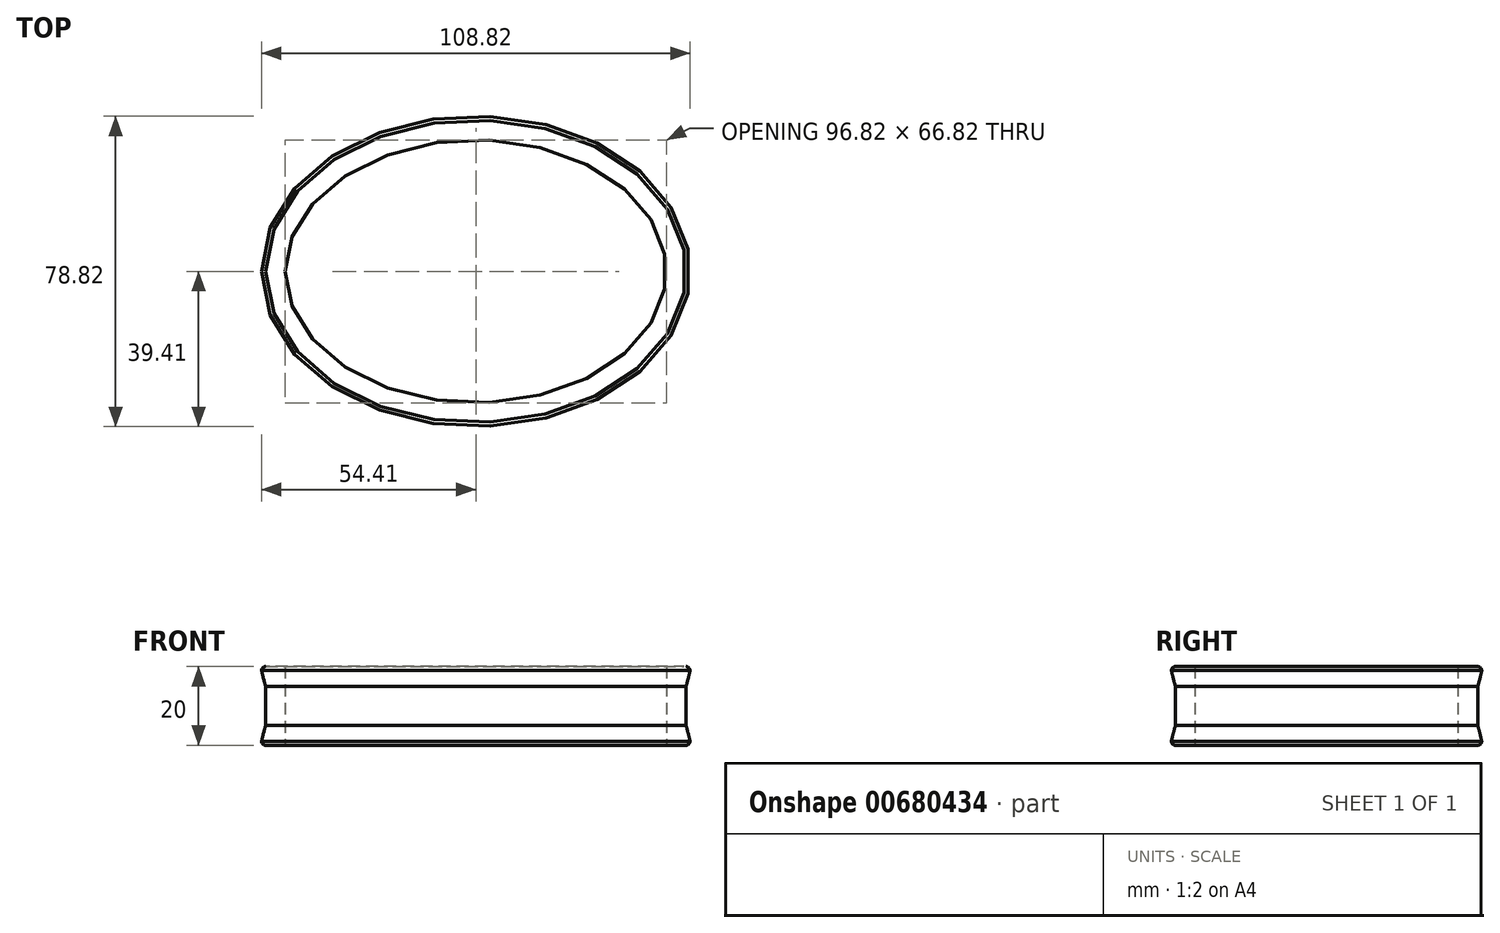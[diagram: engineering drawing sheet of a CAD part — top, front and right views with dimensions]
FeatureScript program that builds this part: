
annotation { "Feature Type Name" : "Feature", "Feature Type Description" : "" }
export const myFeature = defineFeature(function(context is Context, id is Id, definition is map)
    precondition{}
    {
        {
            var Q0;
            Q0=qCreatedBy(makeId("Top.planeOp"),FACE);
            var sketch = newSketch(context, id + "F0", { "sketchPlane" : qUnion([Q0])});
            skEllipse(sketch, "E0", {"center": v(0, 0) * mm, "majorRadius": 50 * mm, "minorRadius": 35 * mm, "majorAxis": v(-1, 0)});
            skSolve(sketch);
        }
        {
            var Q0;
            Q0=qCreatedBy(makeId("Front.planeOp"),FACE);
            var sketch = newSketch(context, id + "F1", { "sketchPlane" : qUnion([Q0])});
            skLineSegment(sketch, "E1.bottom", {"start": v(-53.4, 5) * mm, "end": v(-48.4, 5) * mm});
            skLineSegment(sketch, "E1.top", {"start": v(-53.4, -15) * mm, "end": v(-48.4, -15) * mm});
            skLineSegment(sketch, "E1.left", {"start": v(-53.4, 5) * mm, "end": v(-53.4, -15) * mm});
            skLineSegment(sketch, "E1.right", {"start": v(-48.4, 5) * mm, "end": v(-48.4, -15) * mm});
            skSolve(sketch);
        }
        {
            var Q0;
            Q0=makeQuery(id+"F1.imprint","IMPRINT",FACE,{"disambiguationData":[TD([[makeQuery(id+"F1.imprint","IMPRINT",EDGE,{"derivedFrom":sQuery(id+"F1.wireOp",EDGE,"E1.bottom")}),-1.0]])]});
            var Q1;
            Q1 = qConstructionFilter(qBodyType(qCreatedBy(id + "F0" ,EDGE), BodyType.WIRE), ConstructionObject.NO);
            sweep(context, id + "F2", {"profiles" : qUnion([Q0]), "path" : qUnion([Q1])});
        }
        {
            var Q0;
            Q0=qCreatedBy(makeId("Front.planeOp"),FACE);
            var sketch = newSketch(context, id + "F3", { "sketchPlane" : qUnion([Q0])});
            skCircle(sketch, "E2", {"center": v(-53.4, 4) * mm, "radius": 1 * mm});
            skLineSegment(sketch, "E3", {"start": v(-53.4, 4) * mm, "end": v(0, 4) * mm, "construction": true});
            skSolve(sketch);
        }
        {
            var Q0;
            Q0=qCreatedBy(makeId("Front.planeOp"),FACE);
            var sketch = newSketch(context, id + "F4", { "sketchPlane" : qUnion([Q0])});
            skCircle(sketch, "E4", {"center": v(-53.4, -14) * mm, "radius": 1 * mm});
            skLineSegment(sketch, "E5", {"start": v(-53.4, -14) * mm, "end": v(0, -14) * mm, "construction": true});
            skSolve(sketch);
        }
        {
            var Q0;
            Q0=qCreatedBy(makeId("Front.planeOp"),FACE);
            var sketch = newSketch(context, id + "F5", { "sketchPlane" : qUnion([Q0])});
            skLineSegment(sketch, "E6.bottom", {"start": v(-54.4, 4) * mm, "end": v(-53.4, 4) * mm});
            skLineSegment(sketch, "E6.top", {"start": v(-54.4, 0) * mm, "end": v(-53.4, 0) * mm});
            skLineSegment(sketch, "E6.left", {"start": v(-54.4, 4) * mm, "end": v(-54.4, 0) * mm});
            skLineSegment(sketch, "E6.right", {"start": v(-53.4, 4) * mm, "end": v(-53.4, 0) * mm});
            skSolve(sketch);
        }
        {
            var Q0;
            Q0=qCreatedBy(makeId("Front.planeOp"),FACE);
            var sketch = newSketch(context, id + "F6", { "sketchPlane" : qUnion([Q0])});
            skLineSegment(sketch, "E7.bottom", {"start": v(-54.4, -10) * mm, "end": v(-53.4, -10) * mm});
            skLineSegment(sketch, "E7.top", {"start": v(-54.4, -14) * mm, "end": v(-53.4, -14) * mm});
            skLineSegment(sketch, "E7.left", {"start": v(-54.4, -10) * mm, "end": v(-54.4, -14) * mm});
            skLineSegment(sketch, "E7.right", {"start": v(-53.4, -10) * mm, "end": v(-53.4, -14) * mm});
            skSolve(sketch);
        }
        {
            var Q0;
            Q0 = qSketchRegion(id + "F3", true);
            var Q1;
            Q1 = qSketchRegion(id + "F4", true);
            var Q2;
            Q2 = qConstructionFilter(qBodyType(qCreatedBy(id + "F3" ,EDGE), BodyType.WIRE), ConstructionObject.NO);
            var Q3;
            Q3 = qConstructionFilter(qBodyType(qCreatedBy(id + "F4" ,EDGE), BodyType.WIRE), ConstructionObject.NO);
            var Q4;
            Q4 = qConstructionFilter(qBodyType(qCreatedBy(id + "F0" ,EDGE), BodyType.WIRE), ConstructionObject.NO);
            sweep(context, id + "F7", {"profiles" : qUnion([Q0, Q1]), "surfaceProfiles" : qUnion([Q2, Q3]), "path" : qUnion([Q4])});
        }
        {
            var Q0;
            Q0 = qSketchRegion(id + "F5", true);
            var Q1;
            Q1 = qSketchRegion(id + "F6", true);
            var Q2;
            Q2 = qConstructionFilter(qBodyType(qCreatedBy(id + "F0" ,EDGE), BodyType.WIRE), ConstructionObject.NO);
            sweep(context, id + "F8", {"operationType" : NewBodyOperationType.ADD, "profiles" : qUnion([Q0, Q1]), "path" : qUnion([Q2])});
        }
        {
            var Q0;
            Q0=makeQuery(id+"F8.opSweep","SWEPT_EDGE",EDGE,{"disambiguationData":[OSD([sQuery(id+"F0.wireOp",EDGE,"E0"),sQuery(id+"F5.wireOp",EDGE,"E6.top"),sQuery(id+"F5.wireOp",EDGE,"E6.left")])]});
            var Q1;
            Q1=makeQuery(id+"F8.opSweep","SWEPT_EDGE",EDGE,{"disambiguationData":[OSD([sQuery(id+"F0.wireOp",EDGE,"E0"),sQuery(id+"F6.wireOp",EDGE,"E7.bottom"),sQuery(id+"F6.wireOp",EDGE,"E7.left")])]});
            fillet(context, id + "F9", {"entities" : qUnion([Q0, Q1]), "radius" : 10 * mm, "tangentPropagation" : true, "rho" : .1, "crossSection" : FilletCrossSection.CONIC, "allowEdgeOverflow" : false});
        }
    });
